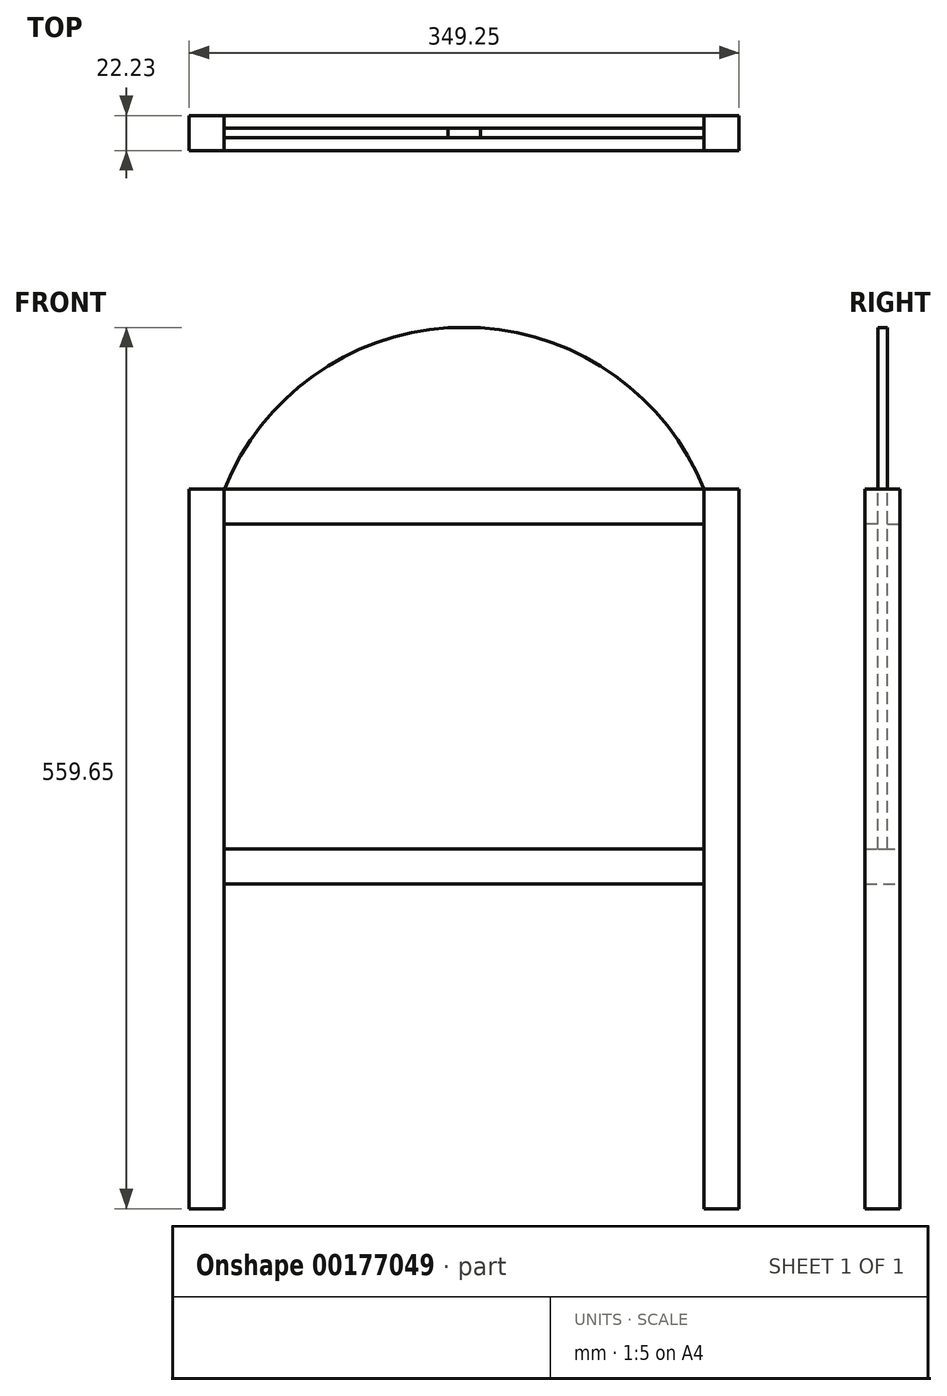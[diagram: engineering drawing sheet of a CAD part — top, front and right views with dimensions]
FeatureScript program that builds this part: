
annotation { "Feature Type Name" : "Feature", "Feature Type Description" : "" }
export const myFeature = defineFeature(function(context is Context, id is Id, definition is map)
    precondition{}
    {
        {
            var Q0;
            Q0=qCreatedBy(makeId("Top.planeOp"),FACE);
            var sketch = newSketch(context, id + "F0", { "sketchPlane" : qUnion([Q0])});
            skLineSegment(sketch, "E0.bottom", {"start": v(50.8, 0) * mm, "end": v(73.03, 0) * mm});
            skLineSegment(sketch, "E0.top", {"start": v(50.8, -22.22) * mm, "end": v(73.03, -22.22) * mm});
            skLineSegment(sketch, "E0.left", {"start": v(50.8, 0) * mm, "end": v(50.8, -22.22) * mm});
            skLineSegment(sketch, "E0.right", {"start": v(73.03, 0) * mm, "end": v(73.03, -22.22) * mm});
            skLineSegment(sketch, "E1.bottom", {"start": v(377.83, 0) * mm, "end": v(400.05, 0) * mm});
            skLineSegment(sketch, "E1.top", {"start": v(377.83, -22.23) * mm, "end": v(400.05, -22.23) * mm});
            skLineSegment(sketch, "E1.left", {"start": v(377.83, 0) * mm, "end": v(377.83, -22.23) * mm});
            skLineSegment(sketch, "E1.right", {"start": v(400.05, 0) * mm, "end": v(400.05, -22.23) * mm});
            skSolve(sketch);
        }
        {
            var Q0;
            Q0 = qSketchRegion(id + "F0", true);
            extrude(context, id + "F1", {"entities" : qUnion([Q0]), "depth" : 457.2 * mm});
        }
        {
            var Q0;
            Q0=makeQuery(id+"F1.opExtrude","SWEPT_FACE",FACE,{"disambiguationData":[OSD([sQuery(id+"F0.wireOp",EDGE,"E0.right")])]});
            var sketch = newSketch(context, id + "F2", { "sketchPlane" : qUnion([Q0])});
            skLineSegment(sketch, "E2.bottom", {"start": v(-22.22, 228.6) * mm, "end": v(0, 228.6) * mm});
            skLineSegment(sketch, "E2.top", {"start": v(-22.23, 206.38) * mm, "end": v(0, 206.38) * mm});
            skLineSegment(sketch, "E2.left", {"start": v(-22.22, 228.6) * mm, "end": v(-22.22, 206.38) * mm});
            skLineSegment(sketch, "E2.right", {"start": v(0, 228.6) * mm, "end": v(0, 206.38) * mm});
            skSolve(sketch);
        }
        {
            var Q0;
            Q0=makeQuery(id+"F2.imprint","IMPRINT",FACE,{"disambiguationData":[TD([[makeQuery(id+"F2.imprint","IMPRINT",EDGE,{"derivedFrom":sQuery(id+"F2.wireOp",EDGE,"E2.bottom")}),-1.0]])]});
            extrude(context, id + "F3", {"entities" : qUnion([Q0]), "endBound" : BoundingType.UP_TO_NEXT, "depth" : 25.4 * mm});
        }
        {
            var Q0;
            Q0=makeQuery(id+"F1.opExtrude","SWEPT_FACE",FACE,{"disambiguationData":[OSD([sQuery(id+"F0.wireOp",EDGE,"E1.left")])]});
            var sketch = newSketch(context, id + "F4", { "sketchPlane" : qUnion([Q0])});
            skPoint(sketch, "E3.firstSnap0", {"position": v(22.23, 228.6) * mm});
            skLineSegment(sketch, "E3.bottom", {"start": v(14.22, 228.6) * mm, "end": v(8.02, 228.6) * mm});
            skLineSegment(sketch, "E3.top", {"start": v(14.22, 559.65) * mm, "end": v(8.02, 559.65) * mm});
            skLineSegment(sketch, "E3.left", {"start": v(14.22, 228.6) * mm, "end": v(14.22, 559.65) * mm});
            skLineSegment(sketch, "E3.right", {"start": v(8.02, 228.6) * mm, "end": v(8.02, 559.65) * mm});
            skLineSegment(sketch, "E4", {"start": v(0, 457.2) * mm, "end": v(8.02, 457.2) * mm});
            skLineSegment(sketch, "E5", {"start": v(22.23, 457.2) * mm, "end": v(14.22, 457.2) * mm});
            skSolve(sketch);
        }
        {
            var Q0;
            {var subQ0=sQuery(id+"F4.wireOp",EDGE,"E3.top");Q0=makeQuery(id+"F4.imprint","IMPRINT",FACE,{"disambiguationData":[TD([[makeQuery(id+"F4.imprint","IMPRINT",EDGE,{"derivedFrom":subQ0}),1.0]])]});}
            var Q1;
            {var subQ0=sQuery(id+"F4.wireOp",EDGE,"E3.bottom");Q1=makeQuery(id+"F4.imprint","IMPRINT",FACE,{"disambiguationData":[TD([[makeQuery(id+"F4.imprint","IMPRINT",EDGE,{"derivedFrom":subQ0}),-1.0]])]});}
            extrude(context, id + "F5", {"entities" : qUnion([Q0, Q1]), "depth" : 304.8 * mm});
        }
        {
            var Q0;
            Q0=makeQuery(id+"F5.opExtrude","SWEPT_FACE",FACE,{"disambiguationData":[OSD([sQuery(id+"F4.wireOp",EDGE,"E3.right")])]});
            var sketch = newSketch(context, id + "F6", { "sketchPlane" : qUnion([Q0])});
            skArc(sketch, "E6", {"start": v(-73.03, 456.75) * mm, "mid": v(-225.43, 559.98) * mm, "end": v(-377.83, 456.75) * mm});
            skSolve(sketch);
        }
        {
            var Q0;
            {var subQ0=sQuery(id+"F6.wireOp",EDGE,"E6");var subQ1=sQuery(id+"F4.wireOp",EDGE,"E3.right");var subQ2=makeQuery(id+"F5.opExtrude","CAP_EDGE",EDGE,{"disambiguationData":[OSD([subQ1])],"isStart":true});var subQ3=makeQuery(id+"F6.imprint","INTERSECT",VERTEX,{"derivedFrom":[subQ2,subQ0]});Q0=makeQuery(id+"F6.imprint","IMPRINT",FACE,{"disambiguationData":[TD([[makeQuery(id+"F6.imprint","IMPRINT",EDGE,{"disambiguationData":[TD([[subQ3,1.0]])],"derivedFrom":subQ0}),-1.0]])]});}
            var Q1;
            {var subQ0=sQuery(id+"F6.wireOp",EDGE,"E6");var subQ1=sQuery(id+"F4.wireOp",EDGE,"E3.right");var subQ2=makeQuery(id+"F5.opExtrude","CAP_EDGE",EDGE,{"disambiguationData":[OSD([subQ1])],"isStart":false});var subQ3=makeQuery(id+"F6.imprint","INTERSECT",VERTEX,{"derivedFrom":[subQ2,subQ0]});Q1=makeQuery(id+"F6.imprint","IMPRINT",FACE,{"disambiguationData":[TD([[makeQuery(id+"F6.imprint","IMPRINT",EDGE,{"disambiguationData":[TD([[subQ3,-1.0]])],"derivedFrom":subQ0}),-1.0]])]});}
            var Q2;
            Q2=makeQuery(id+"F5.opExtrude","SWEPT_FACE",FACE,{"disambiguationData":[OSD([sQuery(id+"F4.wireOp",EDGE,"E3.left")])]});
            extrude(context, id + "F7", {"entities" : qUnion([Q0, Q1]), "operationType" : NewBodyOperationType.REMOVE, "endBound" : BoundingType.UP_TO_SURFACE, "oppositeDirection" : true, "endBoundEntityFace" : qUnion([Q2]), "depth" : 25.4 * mm});
        }
        {
            var Q0;
            Q0=makeQuery(id+"F1.opExtrude","SWEPT_FACE",FACE,{"disambiguationData":[OSD([sQuery(id+"F0.wireOp",EDGE,"E1.left")])]});
            var sketch = newSketch(context, id + "F8", { "sketchPlane" : qUnion([Q0])});
            skLineSegment(sketch, "E7.bottom", {"start": v(0, 457.2) * mm, "end": v(8, 457.2) * mm});
            skLineSegment(sketch, "E7.top", {"start": v(0, 434.98) * mm, "end": v(8, 434.98) * mm});
            skLineSegment(sketch, "E7.left", {"start": v(0, 457.2) * mm, "end": v(0, 434.98) * mm});
            skLineSegment(sketch, "E7.right", {"start": v(8, 457.2) * mm, "end": v(8, 434.98) * mm});
            skLineSegment(sketch, "E8.bottom", {"start": v(22.23, 457.2) * mm, "end": v(14.22, 457.2) * mm});
            skLineSegment(sketch, "E8.top", {"start": v(22.23, 434.98) * mm, "end": v(14.22, 434.98) * mm});
            skLineSegment(sketch, "E8.left", {"start": v(22.23, 457.2) * mm, "end": v(22.23, 434.98) * mm});
            skLineSegment(sketch, "E8.right", {"start": v(14.22, 457.2) * mm, "end": v(14.22, 434.98) * mm});
            skSolve(sketch);
        }
        {
            var Q0;
            Q0=makeQuery(id+"F8.imprint","IMPRINT",FACE,{"disambiguationData":[TD([[makeQuery(id+"F8.imprint","IMPRINT",EDGE,{"derivedFrom":sQuery(id+"F8.wireOp",EDGE,"E8.bottom")}),-1.0]])]});
            var Q1;
            Q1=makeQuery(id+"F8.imprint","IMPRINT",FACE,{"disambiguationData":[TD([[makeQuery(id+"F8.imprint","IMPRINT",EDGE,{"derivedFrom":sQuery(id+"F8.wireOp",EDGE,"E7.bottom")}),-1.0]])]});
            extrude(context, id + "F9", {"entities" : qUnion([Q0, Q1]), "endBound" : BoundingType.UP_TO_NEXT, "depth" : 25.4 * mm});
        }
    });
